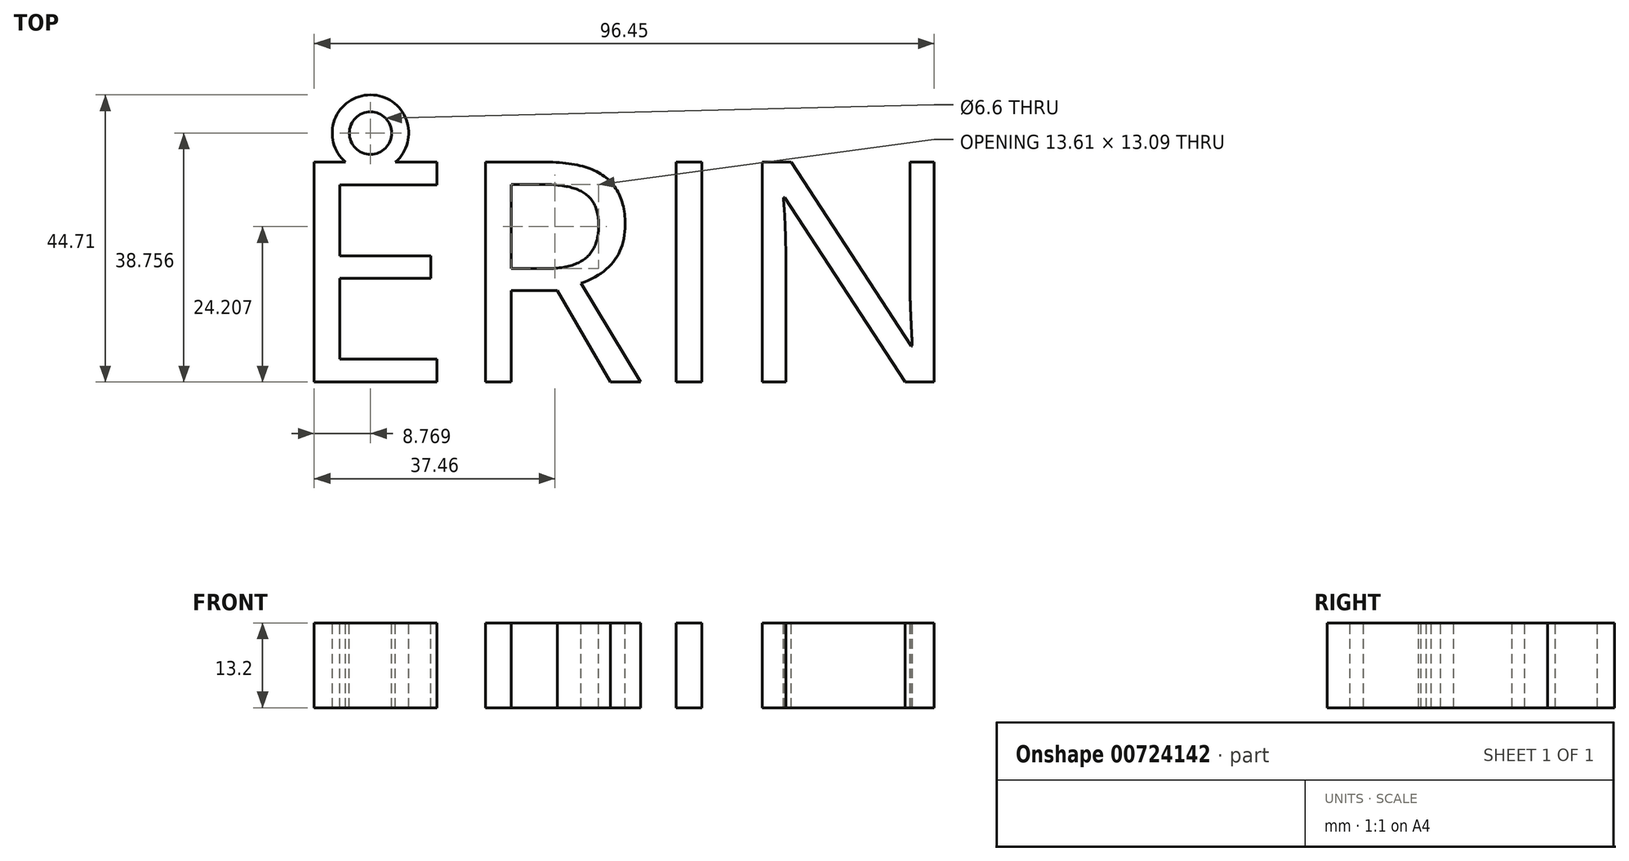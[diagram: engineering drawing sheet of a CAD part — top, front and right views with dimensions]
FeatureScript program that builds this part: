
annotation { "Feature Type Name" : "Feature", "Feature Type Description" : "" }
export const myFeature = defineFeature(function(context is Context, id is Id, definition is map)
    precondition{}
    {
        {
            var Q0;
            Q0=qCreatedBy(makeId("Top.planeOp"),FACE);
            var sketch = newSketch(context, id + "F0", { "sketchPlane" : qUnion([Q0])});
            skText(sketch, "E0", { "text": "ERIN", "fontName": "OpenSans-Regular.ttf"});
            skCircle(sketch, "E1", {"center": v(-40.24, 20.69) * mm, "radius": 5.95 * mm});
            skPoint(sketch, "E1.first.point", {"position": v(-42.6, 26.14) * mm});
            skPoint(sketch, "E1.second.point", {"position": v(-34.7, 18.5) * mm});
            skPoint(sketch, "E1.third.point", {"position": v(-34.44, 22.03) * mm});
            skCircle(sketch, "E2", {"center": v(-40.24, 20.69) * mm, "radius": 3.3 * mm});
            const initialGuessF0  = {"E0": [-0.05372, -0.01807, 1, 0, 0.03454]};
            skSetInitialGuess(sketch, initialGuessF0);
            skSolve(sketch);
        }
        {
            var Q0;
            Q0 = qSketchRegion(id + "F0", true);
            extrude(context, id + "F1", {"entities" : qUnion([Q0]), "oppositeDirection" : true, "depth" : 13.2 * mm, "offsetDistance" : 25 * mm});
        }
    });
